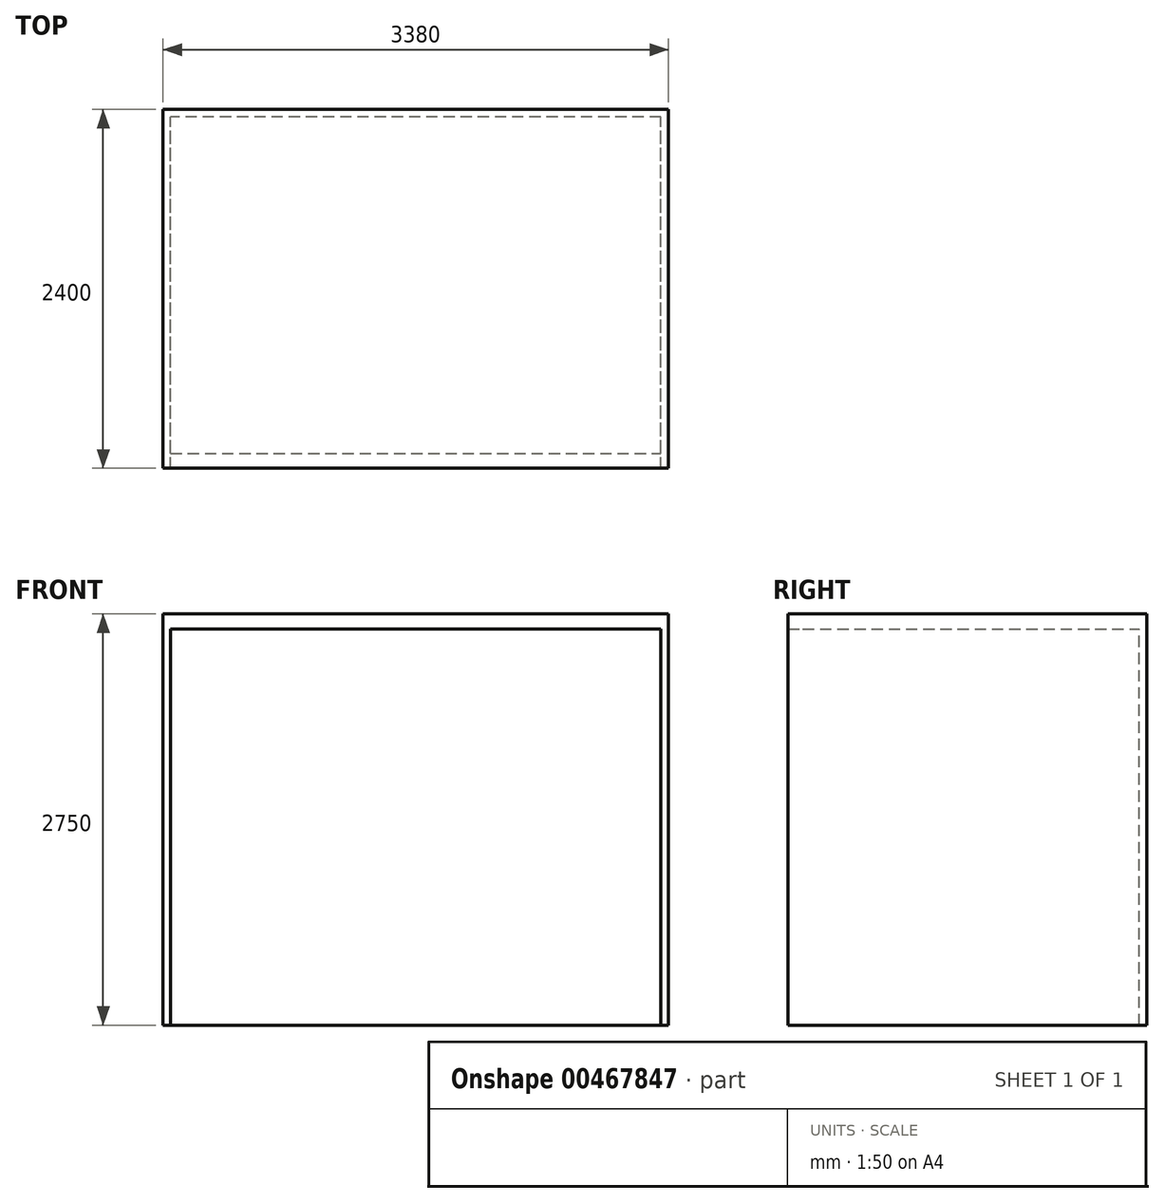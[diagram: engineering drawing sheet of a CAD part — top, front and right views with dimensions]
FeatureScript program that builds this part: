
annotation { "Feature Type Name" : "Feature", "Feature Type Description" : "" }
export const myFeature = defineFeature(function(context is Context, id is Id, definition is map)
    precondition{}
    {
        {
            var Q0;
            Q0=qCreatedBy(makeId("Top.planeOp"),FACE);
            var sketch = newSketch(context, id + "F0", { "sketchPlane" : qUnion([Q0])});
            skLineSegment(sketch, "E0.bottom", {"start": v(1690, -1200) * mm, "end": v(-1690, -1200) * mm});
            skLineSegment(sketch, "E0.top", {"start": v(1690, 1200) * mm, "end": v(-1690, 1200) * mm});
            skLineSegment(sketch, "E0.left", {"start": v(1690, -1200) * mm, "end": v(1690, 1200) * mm});
            skLineSegment(sketch, "E0.right", {"start": v(-1690, -1200) * mm, "end": v(-1690, 1200) * mm});
            skPoint(sketch, "E0.middle", {"position": v(0, 0) * mm});
            skSolve(sketch);
        }
        {
            var Q0;
            Q0=makeQuery(id+"F0.imprint","IMPRINT",FACE,{"disambiguationData":[TD([[makeQuery(id+"F0.imprint","IMPRINT",EDGE,{"derivedFrom":sQuery(id+"F0.wireOp",EDGE,"E0.bottom")}),-1.0]])]});
            extrude(context, id + "F1", {"entities" : qUnion([Q0]), "depth" : 100 * mm});
        }
        {
            var Q0;
            Q0=makeQuery(id+"F1.opExtrude","CAP_FACE",FACE,{"disambiguationData":[OSD([sQuery(id+"F0.wireOp",EDGE,"E0.bottom"),sQuery(id+"F0.wireOp",EDGE,"E0.top"),sQuery(id+"F0.wireOp",EDGE,"E0.left"),sQuery(id+"F0.wireOp",EDGE,"E0.right")])],"isStart":true});
            var sketch = newSketch(context, id + "F2", { "sketchPlane" : qUnion([Q0])});
            skLineSegment(sketch, "E1.bottom", {"start": v(1690, 1200) * mm, "end": v(1640, 1200) * mm});
            skLineSegment(sketch, "E1.top", {"start": v(1690, -1200) * mm, "end": v(1640, -1200) * mm});
            skLineSegment(sketch, "E1.left", {"start": v(1690, 1200) * mm, "end": v(1690, -1200) * mm});
            skLineSegment(sketch, "E1.right", {"start": v(1640, 1200) * mm, "end": v(1640, -1200) * mm});
            skSolve(sketch);
        }
        {
            var Q0;
            Q0=makeQuery(id+"F2.imprint","IMPRINT",FACE,{"disambiguationData":[TD([[makeQuery(id+"F2.imprint","IMPRINT",EDGE,{"derivedFrom":sQuery(id+"F2.wireOp",EDGE,"E1.bottom")}),1.0]])]});
            extrude(context, id + "F3", {"entities" : qUnion([Q0]), "operationType" : NewBodyOperationType.ADD, "depth" : 2650 * mm});
        }
        {
            var Q0;
            Q0=makeQuery(id+"F1.opExtrude","CAP_FACE",FACE,{"disambiguationData":[OSD([sQuery(id+"F0.wireOp",EDGE,"E0.bottom"),sQuery(id+"F0.wireOp",EDGE,"E0.top"),sQuery(id+"F0.wireOp",EDGE,"E0.left"),sQuery(id+"F0.wireOp",EDGE,"E0.right")])],"isStart":true});
            var sketch = newSketch(context, id + "F4", { "sketchPlane" : qUnion([Q0])});
            skLineSegment(sketch, "E2.bottom", {"start": v(1640, -1200) * mm, "end": v(-1690, -1200) * mm});
            skLineSegment(sketch, "E2.top", {"start": v(1640, -1150) * mm, "end": v(-1690, -1150) * mm});
            skLineSegment(sketch, "E2.left", {"start": v(1640, -1200) * mm, "end": v(1640, -1150) * mm});
            skLineSegment(sketch, "E2.right", {"start": v(-1690, -1200) * mm, "end": v(-1690, -1150) * mm});
            skSolve(sketch);
        }
        {
            var Q0;
            Q0=makeQuery(id+"F4.imprint","IMPRINT",FACE,{"disambiguationData":[TD([[makeQuery(id+"F4.imprint","IMPRINT",EDGE,{"derivedFrom":sQuery(id+"F4.wireOp",EDGE,"E2.bottom")}),-1.0]])]});
            extrude(context, id + "F5", {"entities" : qUnion([Q0]), "operationType" : NewBodyOperationType.ADD, "depth" : 2650 * mm});
        }
        {
            var Q0;
            Q0=makeQuery(id+"F1.opExtrude","CAP_FACE",FACE,{"disambiguationData":[OSD([sQuery(id+"F0.wireOp",EDGE,"E0.bottom"),sQuery(id+"F0.wireOp",EDGE,"E0.top"),sQuery(id+"F0.wireOp",EDGE,"E0.left"),sQuery(id+"F0.wireOp",EDGE,"E0.right")])],"isStart":true});
            var sketch = newSketch(context, id + "F6", { "sketchPlane" : qUnion([Q0])});
            skLineSegment(sketch, "E3.bottom", {"start": v(-1690, 1200) * mm, "end": v(-1640, 1200) * mm});
            skLineSegment(sketch, "E3.top", {"start": v(-1690, -1150) * mm, "end": v(-1640, -1150) * mm});
            skLineSegment(sketch, "E3.left", {"start": v(-1690, 1200) * mm, "end": v(-1690, -1150) * mm});
            skLineSegment(sketch, "E3.right", {"start": v(-1640, 1200) * mm, "end": v(-1640, -1150) * mm});
            skSolve(sketch);
        }
        {
            var Q0;
            {var subQ0=sQuery(id+"F6.wireOp",EDGE,"E3.right");Q0=makeQuery(id+"F6.imprint","IMPRINT",FACE,{"disambiguationData":[TD([[makeQuery(id+"F6.imprint","IMPRINT",EDGE,{"derivedFrom":subQ0}),1.0]])]});}
            var sketch = newSketch(context, id + "F7", { "sketchPlane" : qUnion([Q0])});
            skSolve(sketch);
        }
        {
            var Q0;
            Q0=makeQuery(id+"F6.imprint","IMPRINT",FACE,{"disambiguationData":[TD([[makeQuery(id+"F6.imprint","IMPRINT",EDGE,{"derivedFrom":sQuery(id+"F6.wireOp",EDGE,"E3.bottom")}),1.0]])]});
            extrude(context, id + "F8", {"entities" : qUnion([Q0]), "operationType" : NewBodyOperationType.ADD, "depth" : 2650 * mm});
        }
        {
            var Q0;
            {var subQ0=sQuery(id+"F6.wireOp",EDGE,"E3.right");Q0=makeQuery(id+"F7.imprint","IMPRINT",FACE,{"disambiguationData":[TD([[makeQuery(id+"F7.imprint","IMPRINT",EDGE,{"derivedFrom":makeQuery(id+"F6.imprint","IMPRINT",EDGE,{"derivedFrom":subQ0})}),1.0]])]});}
            var sketch = newSketch(context, id + "F9", { "sketchPlane" : qUnion([Q0])});
            skLineSegment(sketch, "E4.bottom", {"start": v(-1640, 1200) * mm, "end": v(1640, 1200) * mm});
            skLineSegment(sketch, "E4.top", {"start": v(-1640, 1100) * mm, "end": v(1640, 1100) * mm});
            skLineSegment(sketch, "E4.left", {"start": v(-1640, 1200) * mm, "end": v(-1640, 1100) * mm});
            skLineSegment(sketch, "E4.right", {"start": v(1640, 1200) * mm, "end": v(1640, 1100) * mm});
            skSolve(sketch);
        }
        {
            var Q0;
            Q0=makeQuery(id+"F9.imprint","IMPRINT",FACE,{"disambiguationData":[TD([[makeQuery(id+"F9.imprint","IMPRINT",EDGE,{"derivedFrom":sQuery(id+"F9.wireOp",EDGE,"E4.bottom")}),1.0]])]});
            extrude(context, id + "F10", {"entities" : qUnion([Q0]), "operationType" : NewBodyOperationType.ADD, "depth" : 0.01 * mm});
        }
    });
